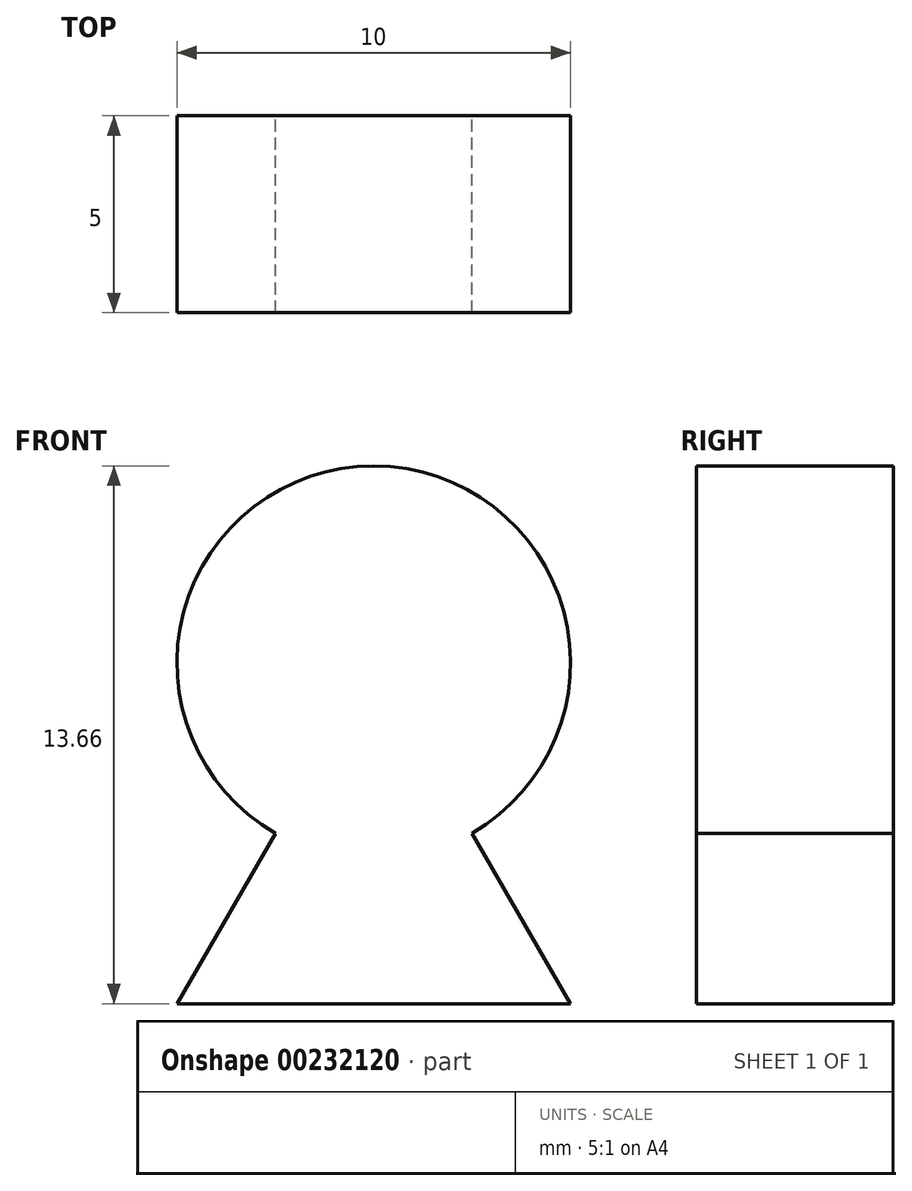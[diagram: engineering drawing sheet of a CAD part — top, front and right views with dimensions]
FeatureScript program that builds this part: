
annotation { "Feature Type Name" : "Feature", "Feature Type Description" : "" }
export const myFeature = defineFeature(function(context is Context, id is Id, definition is map)
    precondition{}
    {
        {
            var Q0;
            Q0=qCreatedBy(makeId("Front.planeOp"),FACE);
            var sketch = newSketch(context, id + "F0", { "sketchPlane" : qUnion([Q0])});
            skArc(sketch, "E0", {"start": v(2.5, -4.33) * mm, "mid": v(0, 5) * mm, "end": v(-2.5, -4.33) * mm});
            skLineSegment(sketch, "E1", {"start": v(-2.5, -4.33) * mm, "end": v(-5, -8.66) * mm});
            skLineSegment(sketch, "E2", {"start": v(-5, -8.66) * mm, "end": v(5, -8.66) * mm});
            skLineSegment(sketch, "E3", {"start": v(5, -8.66) * mm, "end": v(2.5, -4.33) * mm});
            skSolve(sketch);
        }
        {
            var Q0;
            Q0 = qSketchRegion(id + "F0", true);
            extrude(context, id + "F1", {"entities" : qUnion([Q0]), "depth" : 5 * mm});
        }
    });
